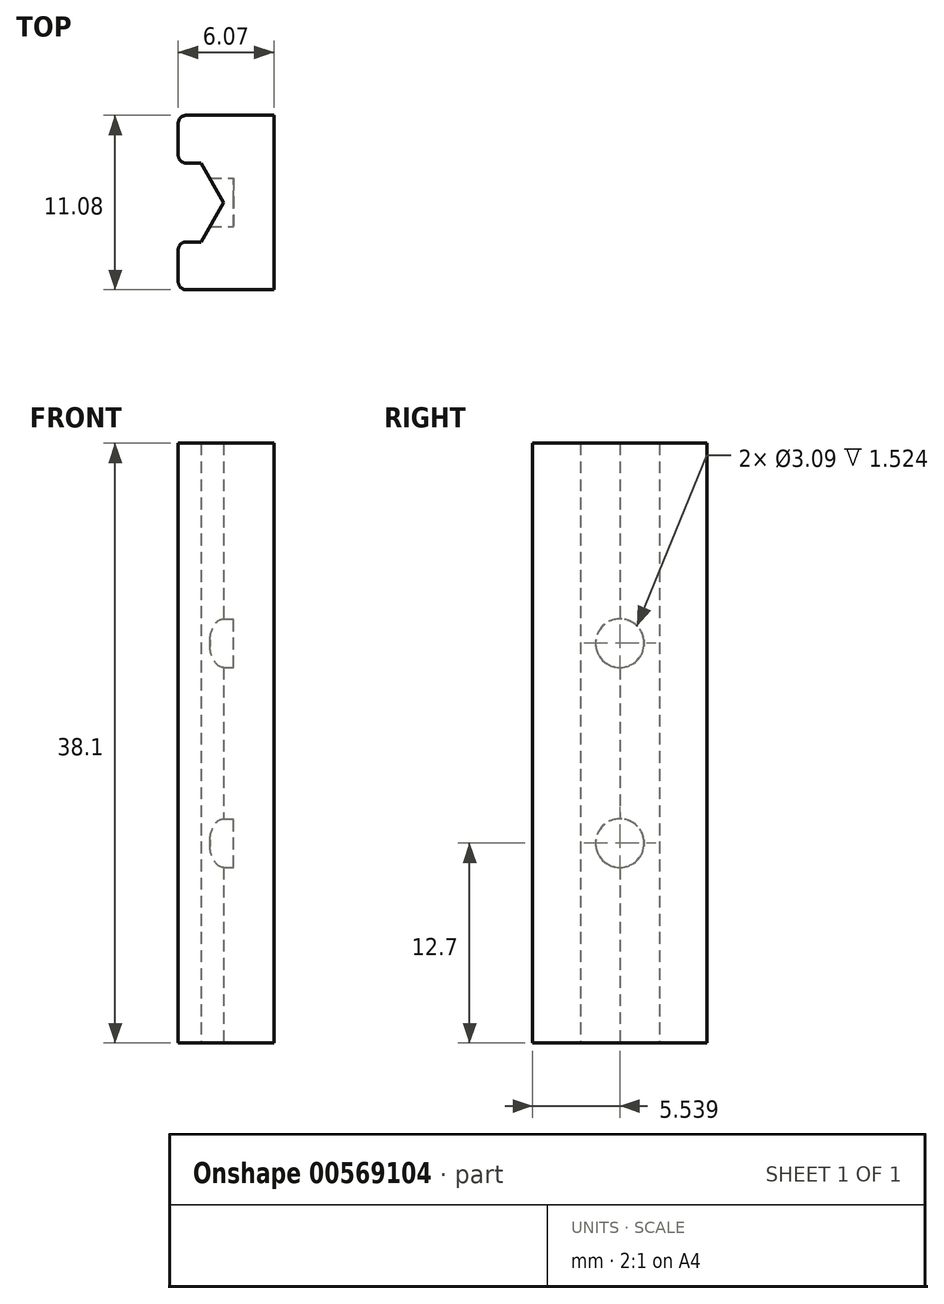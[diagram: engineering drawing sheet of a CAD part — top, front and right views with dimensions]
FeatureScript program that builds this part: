
annotation { "Feature Type Name" : "Feature", "Feature Type Description" : "" }
export const myFeature = defineFeature(function(context is Context, id is Id, definition is map)
    precondition{}
    {
        {
            var Q0;
            Q0=qCreatedBy(makeId("Top.planeOp"),FACE);
            var sketch = newSketch(context, id + "F0", { "sketchPlane" : qUnion([Q0])});
            skLineSegment(sketch, "E0", {"start": v(-19.05, 0) * mm, "end": v(19.05, 0) * mm});
            skLineSegment(sketch, "E1.0", {"start": v(-19.05, 4.98) * mm, "end": v(19.05, 4.98) * mm});
            skLineSegment(sketch, "E2.0", {"start": v(-19.05, 8.03) * mm, "end": v(19.05, 8.03) * mm});
            skLineSegment(sketch, "E3.0", {"start": v(-19.05, -3.05) * mm, "end": v(19.05, -3.05) * mm});
            skLineSegment(sketch, "E4", {"start": v(-19.05, 8.03) * mm, "end": v(-19.05, -3.05) * mm});
            skLineSegment(sketch, "E5.0", {"start": v(19.05, 8.03) * mm, "end": v(19.05, -3.05) * mm});
            skLineSegment(sketch, "E6", {"start": v(-34.77, 8.03) * mm, "end": v(-31.75, 8.03) * mm});
            skLineSegment(sketch, "E7", {"start": v(-34.77, -3.05) * mm, "end": v(-31.75, -3.05) * mm});
            skLineSegment(sketch, "E8", {"start": v(-34.77, 8.03) * mm, "end": v(-34.77, 5) * mm});
            skLineSegment(sketch, "E9.0", {"start": v(-33.33, 5) * mm, "end": v(-31.88, 2.49) * mm});
            skLineSegment(sketch, "E9.1", {"start": v(-31.88, 2.49) * mm, "end": v(-33.33, -0.01) * mm});
            skLineSegment(sketch, "E9.2", {"start": v(-33.33, -0.01) * mm, "end": v(-34.77, -0.01) * mm});
            skLineSegment(sketch, "E9.5", {"start": v(-34.77, 5) * mm, "end": v(-33.33, 5) * mm});
            skLineSegment(sketch, "E10", {"start": v(-31.75, 8.03) * mm, "end": v(-28.7, 8.03) * mm});
            skLineSegment(sketch, "E11", {"start": v(-28.7, 8.03) * mm, "end": v(-28.7, -3.05) * mm});
            skLineSegment(sketch, "E12", {"start": v(-28.7, -3.05) * mm, "end": v(-31.75, -3.05) * mm});
            skLineSegment(sketch, "E13.trimOffspring", {"start": v(-34.77, -0.01) * mm, "end": v(-34.77, -3.05) * mm});
            skLineSegment(sketch, "E14", {"start": v(-19.05, 2.49) * mm, "end": v(19.05, 2.49) * mm});
            skLineSegment(sketch, "E15.0", {"start": v(-6.35, 8.03) * mm, "end": v(-6.35, -3.05) * mm});
            skLineSegment(sketch, "E16.0", {"start": v(19.22, 8.03) * mm, "end": v(19.22, -3.05) * mm});
            skLineSegment(sketch, "E17.0", {"start": v(6.52, 8.03) * mm, "end": v(6.52, -3.05) * mm});
            skCircle(sketch, "E18", {"center": v(-6.35, 2.49) * mm, "radius": 1.54 * mm});
            skCircle(sketch, "E19", {"center": v(6.52, 2.49) * mm, "radius": 1.54 * mm});
            skSolve(sketch);
        }
        {
            var Q0;
            Q0=makeQuery(id+"F0.imprint","IMPRINT",FACE,{"disambiguationData":[TD([[makeQuery(id+"F0.imprint","IMPRINT",EDGE,{"derivedFrom":sQuery(id+"F0.wireOp",EDGE,"E6")}),-1.0]])]});
            extrude(context, id + "F1", {"entities" : qUnion([Q0]), "depth" : 38.1 * mm, "offsetDistance" : 25.4 * mm});
        }
        {
            var Q0;
            Q0=makeQuery(id+"F1.opExtrude","SWEPT_FACE",FACE,{"disambiguationData":[OSD([sQuery(id+"F0.wireOp",EDGE,"E11")])]});
            var sketch = newSketch(context, id + "F2", { "sketchPlane" : qUnion([Q0])});
            skCircle(sketch, "E20", {"center": v(2.49, 12.7) * mm, "radius": 1.54 * mm});
            skCircle(sketch, "E21", {"center": v(2.49, 25.4) * mm, "radius": 1.54 * mm});
            skSolve(sketch);
        }
        {
            var Q0;
            Q0=makeQuery(id+"F2.imprint","IMPRINT",FACE,{"disambiguationData":[TD([[makeQuery(id+"F2.imprint","IMPRINT",EDGE,{"derivedFrom":sQuery(id+"F2.wireOp",EDGE,"E21")}),1.0]])]});
            var Q1;
            Q1=makeQuery(id+"F2.imprint","IMPRINT",FACE,{"disambiguationData":[TD([[makeQuery(id+"F2.imprint","IMPRINT",EDGE,{"derivedFrom":sQuery(id+"F2.wireOp",EDGE,"E20")}),1.0]])]});
            extrude(context, id + "F3", {"entities" : qUnion([Q0, Q1]), "operationType" : NewBodyOperationType.REMOVE, "oppositeDirection" : true, "depth" : 4.06 * mm, "offsetDistance" : 25.4 * mm, "hasSecondDirection" : true, "secondDirectionOppositeDirection" : false, "secondDirectionDepth" : -2.54 * mm});
        }
        {
            var Q0;
            Q0=makeQuery(id+"F1.opExtrude","SWEPT_EDGE",EDGE,{"disambiguationData":[OSD([sQuery(id+"F0.wireOp",EDGE,"E7"),sQuery(id+"F0.wireOp",EDGE,"E13.trimOffspring")])]});
            var Q1;
            Q1=makeQuery(id+"F1.opExtrude","SWEPT_EDGE",EDGE,{"disambiguationData":[OSD([sQuery(id+"F0.wireOp",EDGE,"E6"),sQuery(id+"F0.wireOp",EDGE,"E8")])]});
            var Q2;
            Q2=makeQuery(id+"F1.opExtrude","SWEPT_EDGE",EDGE,{"disambiguationData":[OSD([sQuery(id+"F0.wireOp",EDGE,"E8"),sQuery(id+"F0.wireOp",EDGE,"E9.5")])]});
            var Q3;
            Q3=makeQuery(id+"F1.opExtrude","SWEPT_EDGE",EDGE,{"disambiguationData":[OSD([sQuery(id+"F0.wireOp",EDGE,"E9.2"),sQuery(id+"F0.wireOp",EDGE,"E13.trimOffspring")])]});
            fillet(context, id + "F4", {"entities" : qUnion([Q0, Q1, Q2, Q3]), "radius" : 0.5 * mm, "tangentPropagation" : true, "allowEdgeOverflow" : false});
        }
    });
